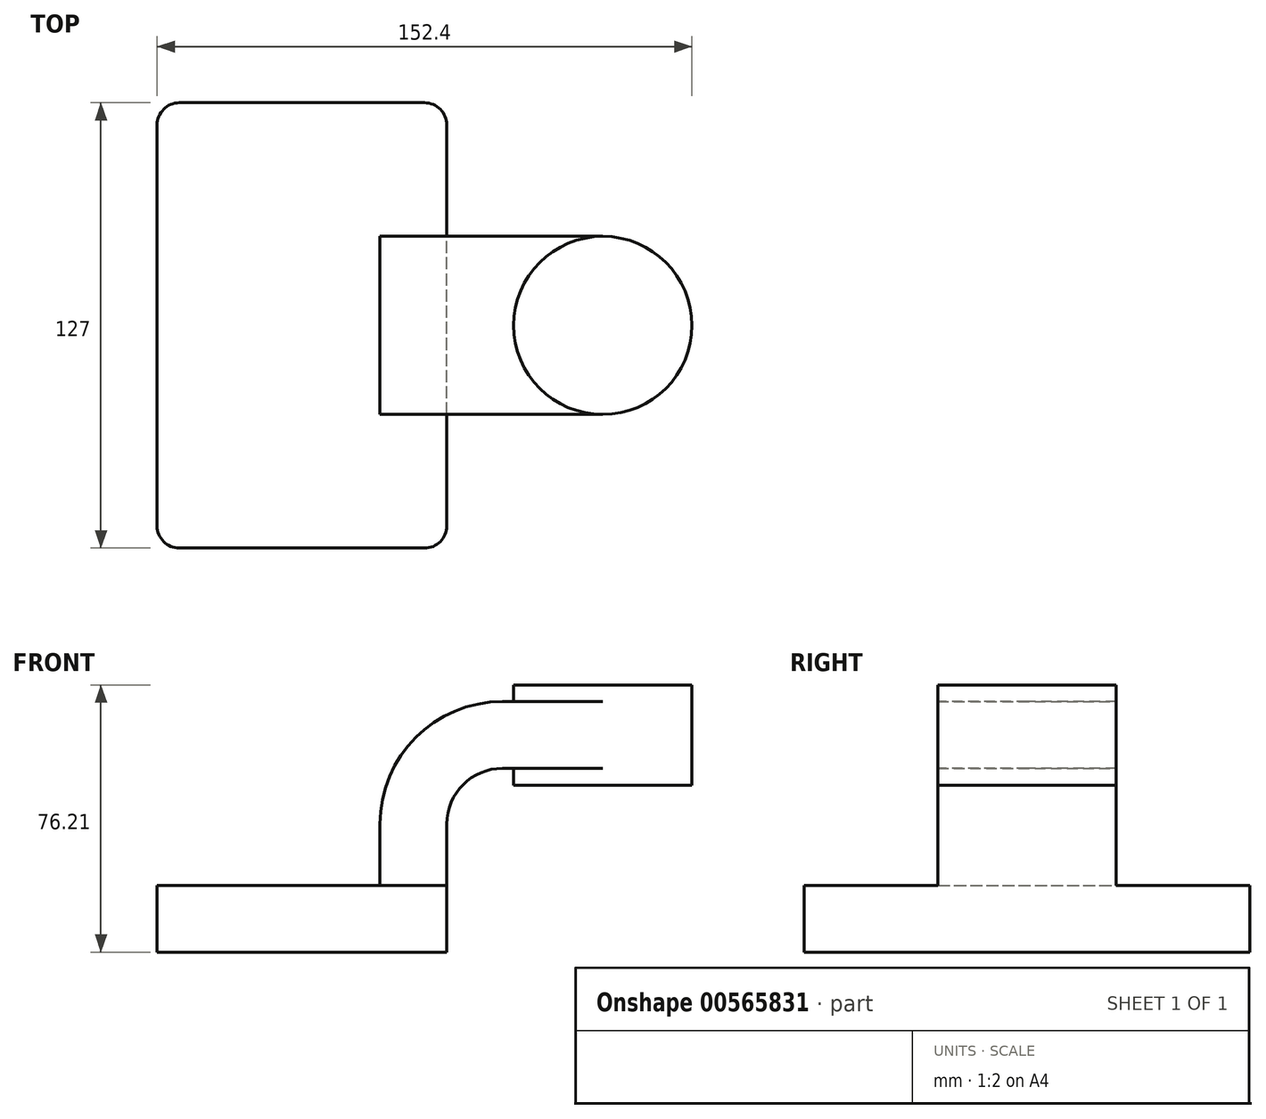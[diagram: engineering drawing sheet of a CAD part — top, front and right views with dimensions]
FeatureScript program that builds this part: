
annotation { "Feature Type Name" : "Feature", "Feature Type Description" : "" }
export const myFeature = defineFeature(function(context is Context, id is Id, definition is map)
    precondition{}
    {
        {
            var Q0;
            Q0=qCreatedBy(makeId("Front.planeOp"),FACE);
            var sketch = newSketch(context, id + "F0", { "sketchPlane" : qUnion([Q0])});
            skLineSegment(sketch, "E0.bottom", {"start": v(-41.28, -9.53) * mm, "end": v(41.28, -9.53) * mm});
            skLineSegment(sketch, "E0.top", {"start": v(-41.28, 9.52) * mm, "end": v(41.28, 9.52) * mm});
            skLineSegment(sketch, "E0.left", {"start": v(-41.27, -9.53) * mm, "end": v(-41.28, 9.52) * mm});
            skLineSegment(sketch, "E0.right", {"start": v(41.28, -9.53) * mm, "end": v(41.28, 9.52) * mm});
            skPoint(sketch, "E0.middle", {"position": v(0, 0) * mm});
            skLineSegment(sketch, "E1.bottom", {"start": v(111.12, 38.1) * mm, "end": v(60.32, 38.1) * mm});
            skLineSegment(sketch, "E1.top", {"start": v(111.12, 66.68) * mm, "end": v(60.32, 66.67) * mm});
            skLineSegment(sketch, "E1.left", {"start": v(111.12, 38.1) * mm, "end": v(111.12, 66.68) * mm});
            skLineSegment(sketch, "E1.right", {"start": v(60.32, 38.1) * mm, "end": v(60.32, 66.68) * mm});
            skPoint(sketch, "E1.middle", {"position": v(85.72, 52.39) * mm});
            skLineSegment(sketch, "E2", {"start": v(41.27, 9.52) * mm, "end": v(41.27, 27) * mm});
            skArc(sketch, "E3", {"start": v(41.27, 27) * mm, "mid": v(45.92, 38.23) * mm, "end": v(57.15, 42.88) * mm});
            skLineSegment(sketch, "E4", {"start": v(57.15, 42.88) * mm, "end": v(85.72, 42.88) * mm});
            skLineSegment(sketch, "E5.0", {"start": v(57.15, 61.93) * mm, "end": v(85.72, 61.93) * mm});
            skArc(sketch, "E5.1", {"start": v(22.23, 27) * mm, "mid": v(32.45, 51.7) * mm, "end": v(57.15, 61.93) * mm});
            skLineSegment(sketch, "E5.2", {"start": v(22.22, 9.52) * mm, "end": v(22.22, 27) * mm});
            skLineSegment(sketch, "E6", {"start": v(85.72, 38.1) * mm, "end": v(85.72, 66.68) * mm});
            skFitSpline(sketch, "E7", {"points": [v(-41.28, 9.53) * mm, v(57.15, 61.93) * mm], "startDerivative": vector(-0.41, 70.8) * mm, "endDerivative": vector(114.72, -16.02) * mm});
            skSolve(sketch);
        }
        {
            var Q0;
            Q0=makeQuery(id+"F0.imprint","IMPRINT",FACE,{"disambiguationData":[TD([[makeQuery(id+"F0.imprint","IMPRINT",EDGE,{"derivedFrom":sQuery(id+"F0.wireOp",EDGE,"E0.bottom")}),1.0]])]});
            extrude(context, id + "F1", {"entities" : qUnion([Q0]), "endBound" : BoundingType.SYMMETRIC, "depth" : 127 * mm, "offsetDistance" : 25.4 * mm});
        }
        {
            var Q0;
            {var subQ1=sQuery(id+"F0.wireOp",EDGE,"E2");Q0=makeQuery(id+"F0.imprint","IMPRINT",FACE,{"disambiguationData":[TD([[makeQuery(id+"F0.imprint","IMPRINT",EDGE,{"derivedFrom":subQ1}),1.0]])]});}
            var Q1;
            {var subQ0=sQuery(id+"F0.wireOp",EDGE,"E4");var subQ1=sQuery(id+"F0.wireOp",EDGE,"E1.right");var subQ2=makeQuery(id+"F0.imprint","INTERSECT",VERTEX,{"derivedFrom":[subQ1,subQ0]});Q1=makeQuery(id+"F0.imprint","IMPRINT",FACE,{"disambiguationData":[TD([[makeQuery(id+"F0.imprint","IMPRINT",EDGE,{"disambiguationData":[TD([[subQ2,-1.0]])],"derivedFrom":subQ1}),-1.0]])]});}
            extrude(context, id + "F2", {"entities" : qUnion([Q0, Q1]), "operationType" : NewBodyOperationType.ADD, "endBound" : BoundingType.SYMMETRIC, "depth" : 50.8 * mm, "offsetDistance" : 25.4 * mm});
        }
        {
            var Q0;
            Q0=makeQuery(id+"F0.imprint","IMPRINT",FACE,{"disambiguationData":[TD([[makeQuery(id+"F0.imprint","IMPRINT",EDGE,{"derivedFrom":sQuery(id+"F0.wireOp",EDGE,"E5.1")}),1.0]])]});
            extrude(context, id + "F3", {"entities" : qUnion([Q0]), "operationType" : NewBodyOperationType.ADD, "endBound" : BoundingType.SYMMETRIC, "depth" : 15.88 * mm, "offsetDistance" : 25.4 * mm});
        }
        {
            var Q0;
            {var subQ4=sQuery(id+"F0.wireOp",EDGE,"E1.left");Q0=makeQuery(id+"F0.imprint","IMPRINT",FACE,{"disambiguationData":[TD([[makeQuery(id+"F0.imprint","IMPRINT",EDGE,{"derivedFrom":subQ4}),1.0]])]});}
            var Q1;
            Q1=sQuery(id+"F0.wireOp",EDGE,"E6");
            revolve(context, id + "F4", {"operationType" : NewBodyOperationType.ADD, "entities" : qUnion([Q0]), "axis" : qUnion([Q1]), "revolveType" : RevolveType.FULL});
        }
        {
            var Q0;
            Q0=makeQuery(id+"F1.opExtrude","CAP_EDGE",EDGE,{"disambiguationData":[OSD([sQuery(id+"F0.wireOp",EDGE,"E0.right")])],"isStart":false});
            var Q1;
            Q1=makeQuery(id+"F1.opExtrude","CAP_EDGE",EDGE,{"disambiguationData":[OSD([sQuery(id+"F0.wireOp",EDGE,"E0.left")])],"isStart":false});
            var Q2;
            Q2=makeQuery(id+"F1.opExtrude","CAP_EDGE",EDGE,{"disambiguationData":[OSD([sQuery(id+"F0.wireOp",EDGE,"E0.right")])],"isStart":true});
            var Q3;
            Q3=makeQuery(id+"F1.opExtrude","CAP_EDGE",EDGE,{"disambiguationData":[OSD([sQuery(id+"F0.wireOp",EDGE,"E0.left")])],"isStart":true});
            fillet(context, id + "F5", {"entities" : qUnion([Q0, Q1, Q2, Q3]), "radius" : 6.35 * mm, "tangentPropagation" : true, "allowEdgeOverflow" : false});
        }
    });
